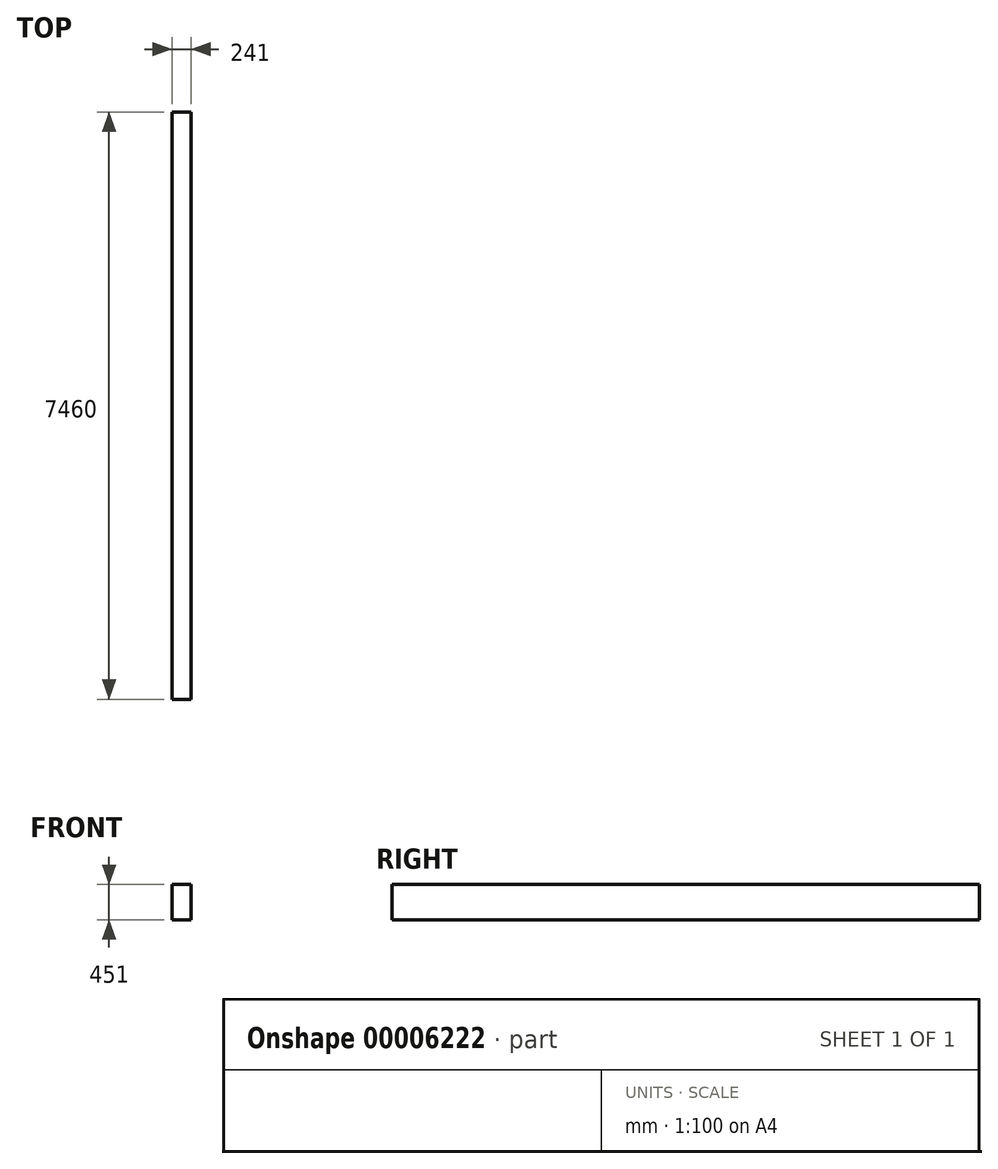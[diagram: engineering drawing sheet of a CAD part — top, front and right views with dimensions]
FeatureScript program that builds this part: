
annotation { "Feature Type Name" : "Feature", "Feature Type Description" : "" }
export const myFeature = defineFeature(function(context is Context, id is Id, definition is map)
    precondition{}
    {
        {
            var Q0;
            Q0=qCreatedBy(makeId("Front.planeOp"),FACE);
            var sketch = newSketch(context, id + "F0", { "sketchPlane" : qUnion([Q0])});
            skPoint(sketch, "E0.rect.middle", {"position": v(0, 0) * mm});
            skLineSegment(sketch, "E1.0", {"start": v(120.5, 225.5) * mm, "end": v(-120.5, 225.5) * mm});
            skLineSegment(sketch, "E1.1", {"start": v(120.5, -225.5) * mm, "end": v(120.5, 225.5) * mm});
            skLineSegment(sketch, "E1.2", {"start": v(120.5, -225.5) * mm, "end": v(-120.5, -225.5) * mm});
            skLineSegment(sketch, "E1.3", {"start": v(-120.5, -225.5) * mm, "end": v(-120.5, 225.5) * mm});
            skPoint(sketch, "E0.rect.left.end.orphan", {"position": v(120, 225) * mm});
            skPoint(sketch, "E0.rect.bottom.start.orphan", {"position": v(120, -225) * mm});
            skPoint(sketch, "E0.rect.right.end.orphan", {"position": v(-120, 225) * mm});
            skPoint(sketch, "E0.rect.right.start.orphan", {"position": v(-120, -225) * mm});
            skSolve(sketch);
        }
        {
            var Q0;
            Q0 = qSketchRegion(id + "F0", true);
            extrude(context, id + "F1", {"entities" : qUnion([Q0]), "depth" : 7460 * mm});
        }
    });
